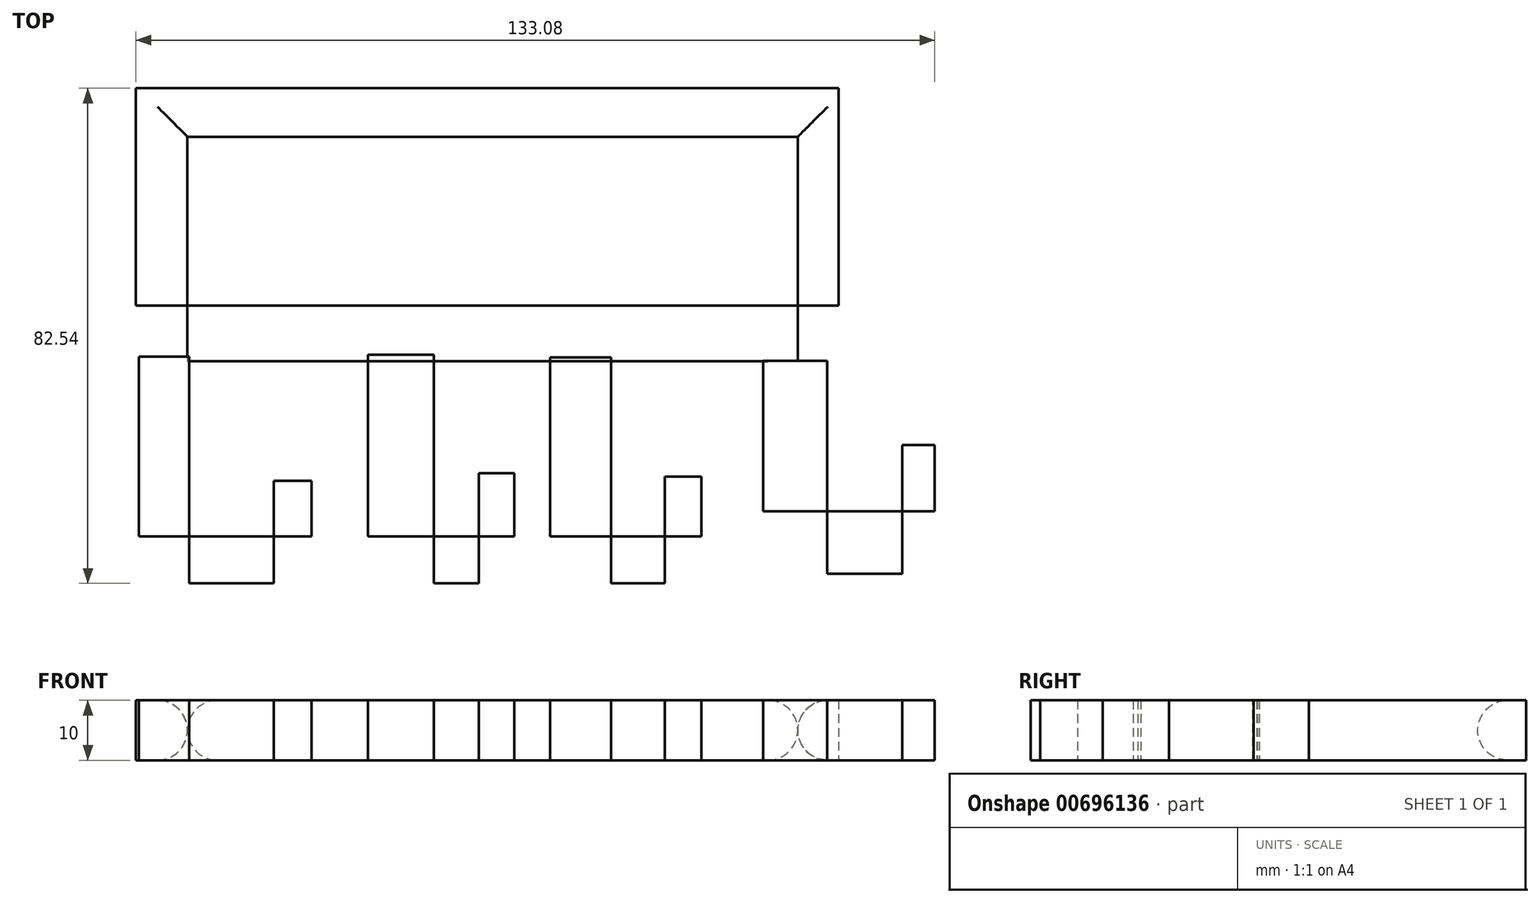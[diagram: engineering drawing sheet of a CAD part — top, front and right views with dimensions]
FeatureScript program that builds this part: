
annotation { "Feature Type Name" : "Feature", "Feature Type Description" : "" }
export const myFeature = defineFeature(function(context is Context, id is Id, definition is map)
    precondition{}
    {
        {
            var Q0;
            Q0=qCreatedBy(makeId("Top.planeOp"),FACE);
            var sketch = newSketch(context, id + "F0", { "sketchPlane" : qUnion([Q0])});
            skLineSegment(sketch, "E0.bottom", {"start": v(-53.1, 36.22) * mm, "end": v(63.4, 36.22) * mm});
            skLineSegment(sketch, "E0.top", {"start": v(-53.1, 28.13) * mm, "end": v(63.4, 28.13) * mm});
            skLineSegment(sketch, "E0.left", {"start": v(-53.1, 36.22) * mm, "end": v(-53.1, 28.13) * mm});
            skLineSegment(sketch, "E0.right", {"start": v(63.4, 36.22) * mm, "end": v(63.4, 28.13) * mm});
            skLineSegment(sketch, "E1.bottom", {"start": v(63.4, 36.22) * mm, "end": v(56.58, 36.22) * mm});
            skLineSegment(sketch, "E1.top", {"start": v(63.4, -9.33) * mm, "end": v(56.58, -9.33) * mm});
            skLineSegment(sketch, "E1.left", {"start": v(63.4, 36.22) * mm, "end": v(63.4, -9.33) * mm});
            skLineSegment(sketch, "E1.right", {"start": v(56.58, 36.22) * mm, "end": v(56.58, -9.33) * mm});
            skLineSegment(sketch, "E2.bottom", {"start": v(63.4, -9.33) * mm, "end": v(-53.68, -9.33) * mm});
            skLineSegment(sketch, "E2.top", {"start": v(63.4, 0) * mm, "end": v(-53.68, 0) * mm});
            skLineSegment(sketch, "E2.left", {"start": v(63.4, -9.33) * mm, "end": v(63.4, 0) * mm});
            skLineSegment(sketch, "E2.right", {"start": v(-53.68, -9.33) * mm, "end": v(-53.68, 0) * mm});
            skLineSegment(sketch, "E3.bottom", {"start": v(-53.68, -9.33) * mm, "end": v(-45.1, -9.33) * mm});
            skLineSegment(sketch, "E3.top", {"start": v(-53.68, 36.22) * mm, "end": v(-45.1, 36.22) * mm});
            skLineSegment(sketch, "E3.left", {"start": v(-53.68, -9.33) * mm, "end": v(-53.68, 36.22) * mm});
            skLineSegment(sketch, "E3.right", {"start": v(-45.1, -9.33) * mm, "end": v(-45.1, 36.22) * mm});
            skSolve(sketch);
        }
        {
            var Q0;
            Q0=qCreatedBy(makeId("Top.planeOp"),FACE);
            var sketch = newSketch(context, id + "F1", { "sketchPlane" : qUnion([Q0])});
            skLineSegment(sketch, "E4.bottom", {"start": v(-53.23, -8.55) * mm, "end": v(-44.82, -8.55) * mm});
            skLineSegment(sketch, "E4.top", {"start": v(-53.23, -46.32) * mm, "end": v(-44.82, -46.32) * mm});
            skLineSegment(sketch, "E4.left", {"start": v(-53.23, -8.55) * mm, "end": v(-53.23, -46.32) * mm});
            skLineSegment(sketch, "E4.right", {"start": v(-44.82, -8.55) * mm, "end": v(-44.82, -46.32) * mm});
            skLineSegment(sketch, "E5.bottom", {"start": v(-15.05, -8.23) * mm, "end": v(-4.05, -8.23) * mm});
            skLineSegment(sketch, "E5.top", {"start": v(-15.05, -46.32) * mm, "end": v(-4.05, -46.32) * mm});
            skLineSegment(sketch, "E5.left", {"start": v(-15.05, -8.23) * mm, "end": v(-15.05, -46.32) * mm});
            skLineSegment(sketch, "E5.right", {"start": v(-4.05, -8.23) * mm, "end": v(-4.05, -46.32) * mm});
            skLineSegment(sketch, "E6.bottom", {"start": v(15.33, -8.66) * mm, "end": v(25.45, -8.66) * mm});
            skLineSegment(sketch, "E6.top", {"start": v(15.33, -46.32) * mm, "end": v(25.45, -46.32) * mm});
            skLineSegment(sketch, "E6.left", {"start": v(15.33, -8.66) * mm, "end": v(15.33, -46.32) * mm});
            skLineSegment(sketch, "E6.right", {"start": v(25.45, -8.66) * mm, "end": v(25.45, -46.32) * mm});
            skLineSegment(sketch, "E7.bottom", {"start": v(50.82, -9.21) * mm, "end": v(61.5, -9.21) * mm});
            skLineSegment(sketch, "E7.top", {"start": v(50.82, -44.76) * mm, "end": v(61.5, -44.76) * mm});
            skLineSegment(sketch, "E7.left", {"start": v(50.82, -9.21) * mm, "end": v(50.82, -44.76) * mm});
            skLineSegment(sketch, "E7.right", {"start": v(61.5, -9.21) * mm, "end": v(61.5, -44.76) * mm});
            skLineSegment(sketch, "E8.bottom", {"start": v(-53.23, -46.32) * mm, "end": v(-24.41, -46.32) * mm});
            skLineSegment(sketch, "E8.top", {"start": v(-53.23, -38.51) * mm, "end": v(-24.41, -38.51) * mm});
            skLineSegment(sketch, "E8.left", {"start": v(-53.23, -46.32) * mm, "end": v(-53.23, -38.51) * mm});
            skLineSegment(sketch, "E8.right", {"start": v(-24.41, -46.32) * mm, "end": v(-24.41, -38.51) * mm});
            skLineSegment(sketch, "E9.bottom", {"start": v(-24.41, -46.32) * mm, "end": v(-30.7, -46.32) * mm});
            skLineSegment(sketch, "E9.top", {"start": v(-24.41, -29.24) * mm, "end": v(-30.7, -29.24) * mm});
            skLineSegment(sketch, "E9.left", {"start": v(-24.41, -46.32) * mm, "end": v(-24.41, -29.24) * mm});
            skLineSegment(sketch, "E9.right", {"start": v(-30.7, -46.32) * mm, "end": v(-30.7, -29.24) * mm});
            skLineSegment(sketch, "E10.bottom", {"start": v(-15.05, -46.32) * mm, "end": v(9.37, -46.32) * mm});
            skLineSegment(sketch, "E10.top", {"start": v(-15.05, -38.51) * mm, "end": v(9.37, -38.51) * mm});
            skLineSegment(sketch, "E10.left", {"start": v(-15.05, -46.32) * mm, "end": v(-15.05, -38.51) * mm});
            skLineSegment(sketch, "E10.right", {"start": v(9.37, -46.32) * mm, "end": v(9.37, -38.51) * mm});
            skLineSegment(sketch, "E11.bottom", {"start": v(9.37, -46.32) * mm, "end": v(3.45, -46.32) * mm});
            skLineSegment(sketch, "E11.top", {"start": v(9.37, -28) * mm, "end": v(3.45, -28) * mm});
            skLineSegment(sketch, "E11.left", {"start": v(9.37, -46.32) * mm, "end": v(9.37, -28) * mm});
            skLineSegment(sketch, "E11.right", {"start": v(3.45, -46.32) * mm, "end": v(3.45, -28) * mm});
            skLineSegment(sketch, "E12.bottom", {"start": v(15.33, -46.32) * mm, "end": v(40.5, -46.32) * mm});
            skLineSegment(sketch, "E12.top", {"start": v(15.33, -38.51) * mm, "end": v(40.5, -38.51) * mm});
            skLineSegment(sketch, "E12.left", {"start": v(15.33, -46.32) * mm, "end": v(15.33, -38.51) * mm});
            skLineSegment(sketch, "E12.right", {"start": v(40.5, -46.32) * mm, "end": v(40.5, -38.51) * mm});
            skLineSegment(sketch, "E13.bottom", {"start": v(40.5, -46.32) * mm, "end": v(34.46, -46.32) * mm});
            skLineSegment(sketch, "E13.top", {"start": v(40.5, -28.51) * mm, "end": v(34.46, -28.51) * mm});
            skLineSegment(sketch, "E13.left", {"start": v(40.5, -46.32) * mm, "end": v(40.5, -28.51) * mm});
            skLineSegment(sketch, "E13.right", {"start": v(34.46, -46.32) * mm, "end": v(34.46, -28.51) * mm});
            skLineSegment(sketch, "E14.bottom", {"start": v(50.82, -44.76) * mm, "end": v(79.4, -44.76) * mm});
            skLineSegment(sketch, "E14.top", {"start": v(50.82, -34.34) * mm, "end": v(79.4, -34.34) * mm});
            skLineSegment(sketch, "E14.left", {"start": v(50.82, -44.76) * mm, "end": v(50.82, -34.34) * mm});
            skLineSegment(sketch, "E14.right", {"start": v(79.4, -44.76) * mm, "end": v(79.4, -34.34) * mm});
            skLineSegment(sketch, "E15.bottom", {"start": v(79.4, -44.76) * mm, "end": v(74.02, -44.76) * mm});
            skLineSegment(sketch, "E15.top", {"start": v(79.4, -23.28) * mm, "end": v(74.02, -23.28) * mm});
            skLineSegment(sketch, "E15.left", {"start": v(79.4, -44.76) * mm, "end": v(79.4, -23.28) * mm});
            skLineSegment(sketch, "E15.right", {"start": v(74.02, -44.76) * mm, "end": v(74.02, -23.28) * mm});
            skSolve(sketch);
        }
        {
            var Q0;
            {var subQ1=sQuery(id+"F0.wireOp",EDGE,"E0.left");Q0=makeQuery(id+"F0.imprint","IMPRINT",FACE,{"disambiguationData":[TD([[makeQuery(id+"F0.imprint","IMPRINT",EDGE,{"derivedFrom":subQ1}),-1.0]])]});}
            var Q1;
            {var subQ0=sQuery(id+"F0.wireOp",EDGE,"E0.left");Q1=makeQuery(id+"F0.imprint","IMPRINT",FACE,{"disambiguationData":[TD([[makeQuery(id+"F0.imprint","IMPRINT",EDGE,{"derivedFrom":subQ0}),1.0]])]});}
            var Q2;
            {var subQ0=sQuery(id+"F0.wireOp",EDGE,"E0.bottom");Q2=makeQuery(id+"F0.imprint","IMPRINT",FACE,{"disambiguationData":[TD([[makeQuery(id+"F0.imprint","IMPRINT",EDGE,{"derivedFrom":subQ0}),-1.0]])]});}
            var Q3;
            {var subQ5=sQuery(id+"F0.wireOp",EDGE,"E1.bottom");Q3=makeQuery(id+"F0.imprint","IMPRINT",FACE,{"disambiguationData":[TD([[makeQuery(id+"F0.imprint","IMPRINT",EDGE,{"derivedFrom":subQ5}),1.0]])]});}
            var Q4;
            {var subQ0=sQuery(id+"F0.wireOp",EDGE,"E1.left");var subQ1=sQuery(id+"F0.wireOp",EDGE,"E0.top");var subQ2=makeQuery(id+"F0.imprint","INTERSECT",VERTEX,{"derivedFrom":[subQ1,subQ0]});Q4=makeQuery(id+"F0.imprint","IMPRINT",FACE,{"disambiguationData":[TD([[makeQuery(id+"F0.imprint","IMPRINT",EDGE,{"disambiguationData":[TD([[subQ2,1.0]])],"derivedFrom":subQ1}),-1.0]])]});}
            var Q5;
            {var subQ5=sQuery(id+"F0.wireOp",EDGE,"E2.left");Q5=makeQuery(id+"F0.imprint","IMPRINT",FACE,{"disambiguationData":[TD([[makeQuery(id+"F0.imprint","IMPRINT",EDGE,{"derivedFrom":subQ5}),1.0]])]});}
            var Q6;
            {var subQ5=sQuery(id+"F0.wireOp",EDGE,"E3.bottom");Q6=makeQuery(id+"F0.imprint","IMPRINT",FACE,{"disambiguationData":[TD([[makeQuery(id+"F0.imprint","IMPRINT",EDGE,{"derivedFrom":subQ5}),1.0]])]});}
            var Q7;
            {var subQ0=sQuery(id+"F0.wireOp",EDGE,"E2.bottom");var subQ1=sQuery(id+"F0.wireOp",EDGE,"E1.right");var subQ2=makeQuery(id+"F0.imprint","INTERSECT",VERTEX,{"derivedFrom":[subQ1,subQ0]});Q7=makeQuery(id+"F0.imprint","IMPRINT",FACE,{"disambiguationData":[TD([[makeQuery(id+"F0.imprint","IMPRINT",EDGE,{"disambiguationData":[TD([[subQ2,1.0]])],"derivedFrom":subQ1}),-1.0]])]});}
            var Q8;
            {var subQ5=sQuery(id+"F1.wireOp",EDGE,"E8.left");Q8=makeQuery(id+"F1.imprint","IMPRINT",FACE,{"disambiguationData":[TD([[makeQuery(id+"F1.imprint","IMPRINT",EDGE,{"derivedFrom":subQ5}),-1.0]])]});}
            var Q9;
            {var subQ0=sQuery(id+"F1.wireOp",EDGE,"E4.bottom");Q9=makeQuery(id+"F1.imprint","IMPRINT",FACE,{"disambiguationData":[TD([[makeQuery(id+"F1.imprint","IMPRINT",EDGE,{"derivedFrom":subQ0}),-1.0]])]});}
            var Q10;
            {var subQ0=sQuery(id+"F1.wireOp",EDGE,"E8.bottom");var subQ1=sQuery(id+"F1.wireOp",EDGE,"E4.right");var subQ2=makeQuery(id+"F1.imprint","INTERSECT",VERTEX,{"derivedFrom":[subQ1,subQ0]});Q10=makeQuery(id+"F1.imprint","IMPRINT",FACE,{"disambiguationData":[TD([[makeQuery(id+"F1.imprint","IMPRINT",EDGE,{"disambiguationData":[TD([[subQ2,1.0]])],"derivedFrom":subQ1}),1.0]])]});}
            var Q11;
            {var subQ5=sQuery(id+"F1.wireOp",EDGE,"E9.bottom");Q11=makeQuery(id+"F1.imprint","IMPRINT",FACE,{"disambiguationData":[TD([[makeQuery(id+"F1.imprint","IMPRINT",EDGE,{"derivedFrom":subQ5}),-1.0]])]});}
            var Q12;
            {var subQ5=sQuery(id+"F1.wireOp",EDGE,"E9.top");Q12=makeQuery(id+"F1.imprint","IMPRINT",FACE,{"disambiguationData":[TD([[makeQuery(id+"F1.imprint","IMPRINT",EDGE,{"derivedFrom":subQ5}),1.0]])]});}
            var Q13;
            {var subQ5=sQuery(id+"F1.wireOp",EDGE,"E10.left");Q13=makeQuery(id+"F1.imprint","IMPRINT",FACE,{"disambiguationData":[TD([[makeQuery(id+"F1.imprint","IMPRINT",EDGE,{"derivedFrom":subQ5}),-1.0]])]});}
            var Q14;
            {var subQ0=sQuery(id+"F1.wireOp",EDGE,"E5.bottom");Q14=makeQuery(id+"F1.imprint","IMPRINT",FACE,{"disambiguationData":[TD([[makeQuery(id+"F1.imprint","IMPRINT",EDGE,{"derivedFrom":subQ0}),-1.0]])]});}
            var Q15;
            {var subQ0=sQuery(id+"F1.wireOp",EDGE,"E10.bottom");var subQ1=sQuery(id+"F1.wireOp",EDGE,"E5.right");var subQ2=makeQuery(id+"F1.imprint","INTERSECT",VERTEX,{"derivedFrom":[subQ1,subQ0]});Q15=makeQuery(id+"F1.imprint","IMPRINT",FACE,{"disambiguationData":[TD([[makeQuery(id+"F1.imprint","IMPRINT",EDGE,{"disambiguationData":[TD([[subQ2,1.0]])],"derivedFrom":subQ1}),1.0]])]});}
            var Q16;
            {var subQ5=sQuery(id+"F1.wireOp",EDGE,"E11.bottom");Q16=makeQuery(id+"F1.imprint","IMPRINT",FACE,{"disambiguationData":[TD([[makeQuery(id+"F1.imprint","IMPRINT",EDGE,{"derivedFrom":subQ5}),-1.0]])]});}
            var Q17;
            {var subQ5=sQuery(id+"F1.wireOp",EDGE,"E11.top");Q17=makeQuery(id+"F1.imprint","IMPRINT",FACE,{"disambiguationData":[TD([[makeQuery(id+"F1.imprint","IMPRINT",EDGE,{"derivedFrom":subQ5}),1.0]])]});}
            var Q18;
            {var subQ5=sQuery(id+"F1.wireOp",EDGE,"E12.left");Q18=makeQuery(id+"F1.imprint","IMPRINT",FACE,{"disambiguationData":[TD([[makeQuery(id+"F1.imprint","IMPRINT",EDGE,{"derivedFrom":subQ5}),-1.0]])]});}
            var Q19;
            {var subQ0=sQuery(id+"F1.wireOp",EDGE,"E6.bottom");Q19=makeQuery(id+"F1.imprint","IMPRINT",FACE,{"disambiguationData":[TD([[makeQuery(id+"F1.imprint","IMPRINT",EDGE,{"derivedFrom":subQ0}),-1.0]])]});}
            var Q20;
            {var subQ0=sQuery(id+"F1.wireOp",EDGE,"E12.bottom");var subQ1=sQuery(id+"F1.wireOp",EDGE,"E6.right");var subQ2=makeQuery(id+"F1.imprint","INTERSECT",VERTEX,{"derivedFrom":[subQ1,subQ0]});Q20=makeQuery(id+"F1.imprint","IMPRINT",FACE,{"disambiguationData":[TD([[makeQuery(id+"F1.imprint","IMPRINT",EDGE,{"disambiguationData":[TD([[subQ2,1.0]])],"derivedFrom":subQ1}),1.0]])]});}
            var Q21;
            {var subQ5=sQuery(id+"F1.wireOp",EDGE,"E13.bottom");Q21=makeQuery(id+"F1.imprint","IMPRINT",FACE,{"disambiguationData":[TD([[makeQuery(id+"F1.imprint","IMPRINT",EDGE,{"derivedFrom":subQ5}),-1.0]])]});}
            var Q22;
            {var subQ5=sQuery(id+"F1.wireOp",EDGE,"E13.top");Q22=makeQuery(id+"F1.imprint","IMPRINT",FACE,{"disambiguationData":[TD([[makeQuery(id+"F1.imprint","IMPRINT",EDGE,{"derivedFrom":subQ5}),1.0]])]});}
            var Q23;
            {var subQ0=sQuery(id+"F1.wireOp",EDGE,"E7.bottom");Q23=makeQuery(id+"F1.imprint","IMPRINT",FACE,{"disambiguationData":[TD([[makeQuery(id+"F1.imprint","IMPRINT",EDGE,{"derivedFrom":subQ0}),-1.0]])]});}
            var Q24;
            {var subQ5=sQuery(id+"F1.wireOp",EDGE,"E14.left");Q24=makeQuery(id+"F1.imprint","IMPRINT",FACE,{"disambiguationData":[TD([[makeQuery(id+"F1.imprint","IMPRINT",EDGE,{"derivedFrom":subQ5}),-1.0]])]});}
            var Q25;
            {var subQ0=sQuery(id+"F1.wireOp",EDGE,"E14.bottom");var subQ1=sQuery(id+"F1.wireOp",EDGE,"E7.right");var subQ2=makeQuery(id+"F1.imprint","INTERSECT",VERTEX,{"derivedFrom":[subQ1,subQ0]});Q25=makeQuery(id+"F1.imprint","IMPRINT",FACE,{"disambiguationData":[TD([[makeQuery(id+"F1.imprint","IMPRINT",EDGE,{"disambiguationData":[TD([[subQ2,1.0]])],"derivedFrom":subQ1}),1.0]])]});}
            var Q26;
            {var subQ5=sQuery(id+"F1.wireOp",EDGE,"E15.bottom");Q26=makeQuery(id+"F1.imprint","IMPRINT",FACE,{"disambiguationData":[TD([[makeQuery(id+"F1.imprint","IMPRINT",EDGE,{"derivedFrom":subQ5}),-1.0]])]});}
            var Q27;
            {var subQ5=sQuery(id+"F1.wireOp",EDGE,"E15.top");Q27=makeQuery(id+"F1.imprint","IMPRINT",FACE,{"disambiguationData":[TD([[makeQuery(id+"F1.imprint","IMPRINT",EDGE,{"derivedFrom":subQ5}),1.0]])]});}
            extrude(context, id + "F2", {"entities" : qUnion([Q0, Q1, Q2, Q3, Q4, Q5, Q6, Q7, Q8, Q9, Q10, Q11, Q12, Q13, Q14, Q15, Q16, Q17, Q18, Q19, Q20, Q21, Q22, Q23, Q24, Q25, Q26, Q27]), "depth" : 10 * mm, "offsetDistance" : 25 * mm});
        }
        {
            var Q0;
            Q0=makeQuery(id+"F2.opExtrude","CAP_EDGE",EDGE,{"disambiguationData":[OSD([sQuery(id+"F0.wireOp",EDGE,"E3.right")])],"isStart":true});
            var Q1;
            Q1=makeQuery(id+"F2.opExtrude","CAP_EDGE",EDGE,{"disambiguationData":[OSD([sQuery(id+"F0.wireOp",EDGE,"E0.top")])],"isStart":true});
            var Q2;
            Q2=makeQuery(id+"F2.opExtrude","CAP_EDGE",EDGE,{"disambiguationData":[OSD([sQuery(id+"F0.wireOp",EDGE,"E1.right")])],"isStart":false});
            var Q3;
            Q3=makeQuery(id+"F2.opExtrude","CAP_EDGE",EDGE,{"disambiguationData":[OSD([sQuery(id+"F0.wireOp",EDGE,"E0.top")])],"isStart":false});
            var Q4;
            Q4=makeQuery(id+"F2.opExtrude","CAP_EDGE",EDGE,{"disambiguationData":[OSD([sQuery(id+"F0.wireOp",EDGE,"E3.right")])],"isStart":false});
            var Q5;
            Q5=makeQuery(id+"F2.opExtrude","CAP_EDGE",EDGE,{"disambiguationData":[OSD([sQuery(id+"F0.wireOp",EDGE,"E1.right")])],"isStart":true});
            fillet(context, id + "F3", {"entities" : qUnion([Q0, Q1, Q2, Q3, Q4, Q5]), "radius" : 5 * mm, "tangentPropagation" : true, "allowEdgeOverflow" : false});
        }
    });
